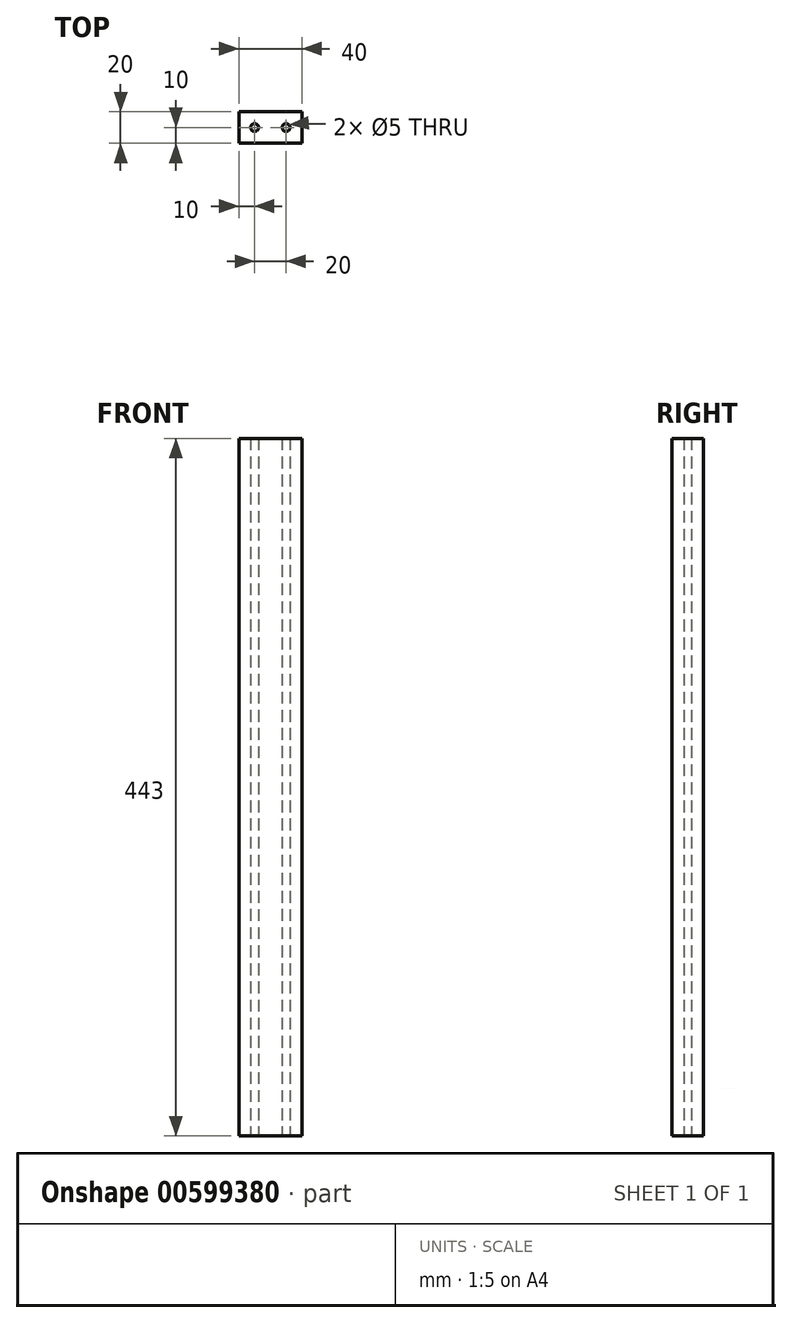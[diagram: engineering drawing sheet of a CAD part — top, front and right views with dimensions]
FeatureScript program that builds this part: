
annotation { "Feature Type Name" : "Feature", "Feature Type Description" : "" }
export const myFeature = defineFeature(function(context is Context, id is Id, definition is map)
    precondition{}
    {
        {
            var Q0;
            Q0=qCreatedBy(makeId("Top.planeOp"),FACE);
            var sketch = newSketch(context, id + "F0", { "sketchPlane" : qUnion([Q0])});
            skLineSegment(sketch, "E0.bottom", {"start": v(-20, 10) * mm, "end": v(20, 10) * mm});
            skLineSegment(sketch, "E0.top", {"start": v(-20, -10) * mm, "end": v(20, -10) * mm});
            skLineSegment(sketch, "E0.left", {"start": v(-20, 10) * mm, "end": v(-20, -10) * mm});
            skLineSegment(sketch, "E0.right", {"start": v(20, 10) * mm, "end": v(20, -10) * mm});
            skCircle(sketch, "E1", {"center": v(-10, 0) * mm, "radius": 2.5 * mm});
            skCircle(sketch, "E2", {"center": v(10, 0) * mm, "radius": 2.5 * mm});
            skSolve(sketch);
        }
        {
            var Q0;
            Q0=qSketchRegion(id+"F0",true);
            extrude(context, id + "F1", {"entities" : qUnion([Q0]), "depth" : 443 * mm, "offsetDistance" : 25 * mm});
        }
        {
            var Q0;
            Q0=makeQuery(id+"F1.opExtrude","SWEPT_FACE",FACE,{"disambiguationData":[OSD([sQuery(id+"F0.wireOp",EDGE,"E0.right")])]});
            var sketch = newSketch(context, id + "F2", { "sketchPlane" : qUnion([Q0])});
            skCircle(sketch, "E3", {"center": v(0, 10) * mm, "radius": 2.5 * mm});
            skSolve(sketch);
        }
        {
            var Q0;
            Q0=makeQuery(id+"F1.opExtrude","SWEPT_FACE",FACE,{"disambiguationData":[OSD([sQuery(id+"F0.wireOp",EDGE,"E0.top")])]});
            var sketch = newSketch(context, id + "F3", { "sketchPlane" : qUnion([Q0])});
            skCircle(sketch, "E4", {"center": v(0, 221.5) * mm, "radius": 2.5 * mm});
            skPoint(sketch, "E4.centerSnap0", {"position": v(-20, 221.5) * mm});
            skSolve(sketch);
        }
        {
            var Q0;
            Q0=makeQuery(id+"F3.imprint","IMPRINT",FACE,{"disambiguationData":[TD([[makeQuery(id+"F3.imprint","IMPRINT",EDGE,{"derivedFrom":sQuery(id+"F3.wireOp",EDGE,"E4")}),-1.0]])]});
            var sketch = newSketch(context, id + "F4", { "sketchPlane" : qUnion([Q0])});
            skCircle(sketch, "E5", {"center": v(10, 10) * mm, "radius": 2.5 * mm});
            skCircle(sketch, "E6", {"center": v(10, 433) * mm, "radius": 2.5 * mm});
            skSolve(sketch);
        }
    });
